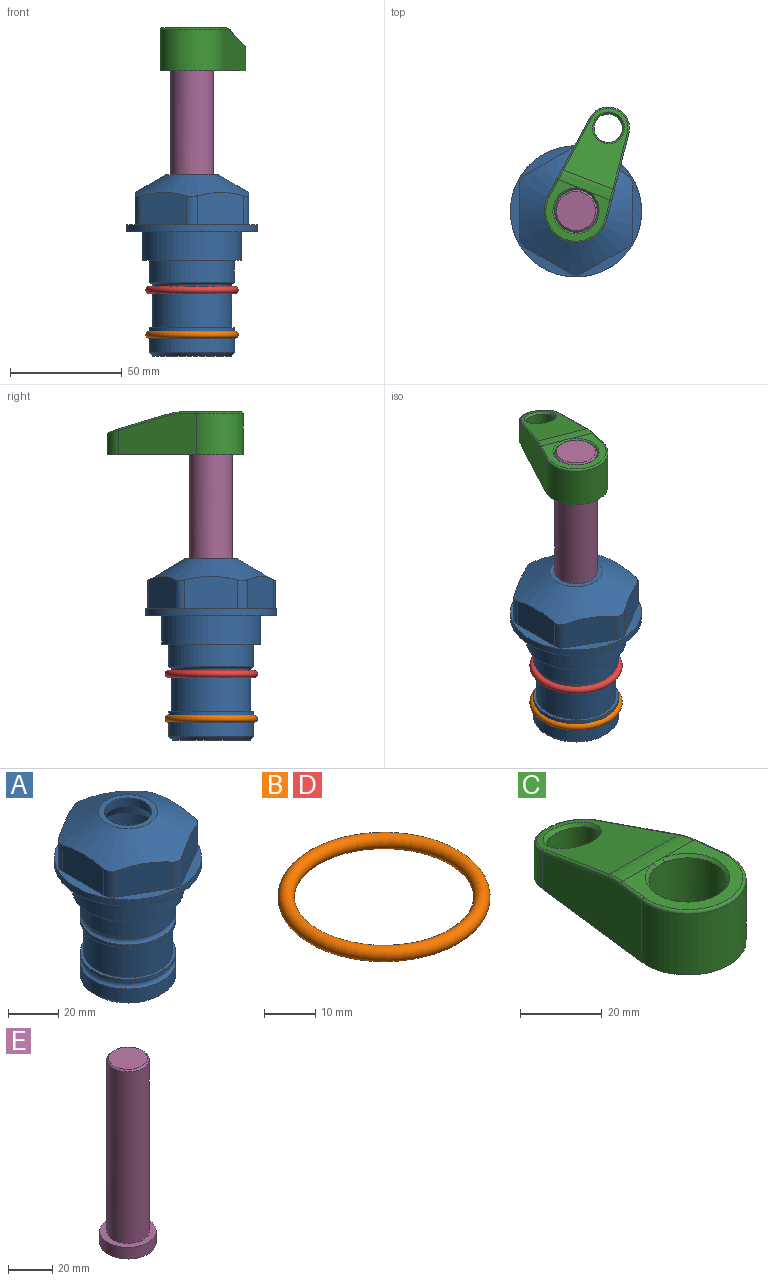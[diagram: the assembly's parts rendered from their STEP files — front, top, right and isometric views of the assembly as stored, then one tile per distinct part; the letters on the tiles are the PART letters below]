
ASSEMBLY  parts=5 mates=4
PART A: 36 faces, bbox 58.7x58.7x81 mm
  f0: cylinder r=17.78mm len=35.56mm, axis (0,0,1), area 1670.8mm2, adj f23,f24,f31
  f1: cylinder r=19.05mm len=38.1mm, axis (0,0,1), area 1191.9mm2, adj f26,f27,f30
  f2: plane 58.66x58.66mm, normal (0,0,-1), area 1150.6mm2, adj f3,f28
  f3: cylinder r=29.33mm len=58.66mm, axis (0,0,-1), area 585.1mm2, adj f2,f4
  f4: plane 58.66x58.66mm, normal (0,0,1), area 475.9mm2, adj f3,f5,f6,f7,f8,f9,f10,f11
  f5: plane 20.32x14.34mm, normal (-0.5,0.87,0), area 324.4mm2, adj f4,f15,f16,f17
  f6: plane 20.32x14.34mm, normal (0.5,0.87,0), area 324.4mm2, adj f4,f14,f15,f17
  f7: plane 23.48x14.34mm, normal (1,0,0), area 324.4mm2, adj f4,f13,f14,f17
  f8: plane 20.32x14.34mm, normal (0.5,-0.87,0), area 324.4mm2, adj f4,f12,f13,f17
  f9: plane 20.32x14.34mm, normal (-0.5,-0.87,0), area 324.4mm2, adj f4,f11,f12,f17
  f10: plane 23.48x14.34mm, normal (-1,0,0), area 324.4mm2, adj f4,f11,f16,f17
  f11: cylinder r=5.08mm len=12.85mm, axis (0,0,-1), area 67.2mm2, adj f4,f9,f10,f17
  f12: cylinder r=5.08mm len=12.85mm, axis (0,0,-1), area 67.2mm2, adj f4,f8,f9,f17
  f13: cylinder r=5.08mm len=12.85mm, axis (0,0,-1), area 67.2mm2, adj f4,f7,f8,f17
  f14: cylinder r=5.08mm len=12.85mm, axis (0,0,-1), area 67.2mm2, adj f4,f6,f7,f17
  f15: cylinder r=5.08mm len=12.85mm, axis (0,0,-1), area 67.2mm2, adj f4,f5,f6,f17
  f16: cylinder r=5.08mm len=12.85mm, axis (0,0,-1), area 67.2mm2, adj f4,f5,f10,f17
  f17: cone r=11.73mm half-angle=60deg, axis (0,0,-1), area 2071.8mm2, adj f5,f6,f7,f8,f9,f10,f11,f12
  f18: plane 23.46x23.46mm, normal (0,0,1), area 147.4mm2, adj f17,f35
  f19: plane 34.93x34.93mm, normal (0,0,-1), area 958mm2, adj f29
  f20: cylinder r=19.05mm len=38.1mm, axis (0,0,1), area 760.1mm2, adj f21,f29
  f21: torus R=19.05mm, axis (0,0,1), area 565.3mm2, adj f20,f22
  f22: cylinder r=19.05mm len=38.1mm, axis (0,0,1), area 190mm2, adj f21,f23
  f23: plane 38.1x38.1mm, normal (0,0,1), area 146.9mm2, adj f0,f22
  f24: plane 38.1x38.1mm, normal (0,0,-1), area 146.9mm2, adj f0,f25
  f25: cylinder r=19.05mm len=38.1mm, axis (0,0,1), area 190mm2, adj f24,f26
  f26: torus R=19.05mm, axis (0,0,1), area 565.3mm2, adj f1,f25
  f27: plane 44.45x44.45mm, normal (0,0,-1), area 411.7mm2, adj f1,f28
  f28: cylinder r=22.23mm len=44.45mm, axis (0,0,1), area 1773.5mm2, adj f2,f27
  f29: cone r=19.05mm half-angle=45deg, axis (0,0,1), area 257.5mm2, adj f19,f20
  f30: cylinder r=3.17mm len=6.75mm, axis (-1,0,0), area 128mm2, adj f1,f33
  f31: cylinder r=3.17mm len=6.35mm, axis (-1,0,0), area 102.5mm2, adj f0,f33
  f32: plane 25.4x25.4mm, normal (0,0,1), area 506.7mm2, adj f33
  f33: cylinder r=12.7mm len=66.42mm, axis (0,0,-1), area 5236.2mm2, adj f30,f31,f32,f34
  f34: cone r=9.53mm half-angle=30deg, axis (0,0,-1), area 443.4mm2, adj f33,f35
  f35: cylinder r=9.53mm len=19.05mm, axis (0,0,-1), area 240.9mm2, adj f18,f34
PART B: 1 faces, bbox 44.7x44.7x3.2 mm
  f0: torus R=19.05mm, axis (0,0,1), area 1193.9mm2
PART C: 31 faces, bbox 31.7x65.5x19.8 mm
  f0: plane 39.12x18.26mm, normal (0.99,0.12,0), area 612.2mm2, adj f1,f4,f7,f11,f13,f15
  f1: cylinder r=9.53mm len=18.91mm, axis (0,0,-1), area 296.1mm2, adj f0,f2,f7,f17
  f2: plane 39.12x18.26mm, normal (-0.99,0.12,0), area 612.2mm2, adj f1,f4,f7,f12,f14,f16
  f3: cylinder r=6.35mm len=12.7mm, axis (0,0,-1), area 362.4mm2, adj f7,f18
  f4: cylinder r=14.29mm len=28.58mm, axis (0,0,-1), area 882.2mm2, adj f0,f2,f7,f10
  f5: cylinder r=9.53mm len=19.05mm, axis (0,0,-1), area 1092.6mm2, adj f7,f19,f20
  f6: plane 26.99x23.69mm, normal (0,0,1), area 216.2mm2, adj f9,f10,f11,f12,f19
  f7: plane 63.5x28.58mm, normal (0,0,-1), area 661.8mm2, adj f0,f1,f2,f3,f4,f5,f22,f23
  f8: plane 33.52x23.6mm, normal (0,0.26,0.97), area 486mm2, adj f9,f15,f16,f17,f18
  f9: cylinder r=19.05mm len=24.72mm, axis (1,0,0), area 120.4mm2, adj f6,f8,f13,f14,f20
  f10: torus R=13.49mm, axis (0,0,1), area 59mm2, adj f4,f6,f11,f12
  f11: cylinder r=0.79mm len=8.67mm, axis (0.12,-0.99,0), area 10.8mm2, adj f0,f6,f10,f13
  f12: cylinder r=0.79mm len=8.67mm, axis (0.12,0.99,0), area 10.8mm2, adj f2,f6,f10,f14
  f13: bspline ~4.95x1.42mm, area 6.1mm2, adj f0,f9,f11,f15
  f14: bspline ~4.95x1.42mm, area 6.1mm2, adj f2,f9,f12,f16
  f15: cylinder r=0.79mm len=25.95mm, axis (0.12,-0.96,0.26), area 32.9mm2, adj f0,f8,f13,f17
  f16: cylinder r=0.79mm len=25.95mm, axis (0.12,0.96,-0.26), area 32.9mm2, adj f2,f8,f14,f17
  f17: bspline ~18.91x8.38mm, area 30mm2, adj f1,f8,f15,f16
  f18: bspline ~14.29x14.29mm, area 48.3mm2, adj f3,f8
  f19: cone r=9.53mm half-angle=45deg, axis (0,0,1), area 66.5mm2, adj f5,f6,f20
  f20: bspline ~3.22x0.96mm, area 3.5mm2, adj f5,f9,f19
  f21: plane 2.75x2.72mm, normal (0,0,-1), area 2.9mm2, adj f23,f25,f28
  f22: plane 23.05x15.88mm, normal (-0.99,-0.12,0), area 323.6mm2, adj f7,f25,f26,f27,f28,f29
  f23: plane 23.05x15.88mm, normal (0.99,-0.12,0), area 323.6mm2, adj f7,f21,f25,f27,f28,f30
  f24: cylinder r=9.53mm len=10.69mm, axis (0,0,-1), area 114.7mm2, adj f7,f27,f29,f30
  f25: cylinder r=12.7mm len=20.59mm, axis (0,0,-1), area 381.1mm2, adj f7,f21,f22,f23,f26,f28
  f26: plane 2.75x2.72mm, normal (0,0,-1), area 2.9mm2, adj f22,f25,f28
  f27: plane 19.72x18.37mm, normal (0,-0.26,-0.97), area 291.8mm2, adj f22,f23,f24,f28,f29,f30
  f28: cylinder r=15.88mm len=19.92mm, axis (1,0,0), area 54.8mm2, adj f21,f22,f23,f25,f26,f27
  f29: cylinder r=1.59mm len=11mm, axis (0,0,-1), area 34.7mm2, adj f7,f22,f24,f27
  f30: cylinder r=1.59mm len=11mm, axis (0,0,-1), area 34.7mm2, adj f7,f23,f24,f27
PART D: same geometry as B
PART E: 6 faces, bbox 25.4x25.4x101.6 mm
  f0: plane 17.46x17.46mm, normal (0,0,1), area 239.5mm2, adj f5
  f1: plane 25.4x25.4mm, normal (0,0,-1), area 506.7mm2, adj f2
  f2: cylinder r=12.7mm len=25.4mm, axis (0,0,1), area 506.7mm2, adj f1,f3
  f3: plane 25.4x25.4mm, normal (0,0,1), area 221.7mm2, adj f2,f4
  f4: cylinder r=9.53mm len=94.46mm, axis (0,0,1), area 5653mm2, adj f3,f5
  f5: cone r=8.73mm half-angle=45deg, axis (0,0,-1), area 64.4mm2, adj f0,f4
PLACE A at identity fixed
PLACE B t=(0,0,-21.59)mm
PLACE C rot(axis=(0,0,-1),21.3deg) t=(0,0,27.55)mm
PLACE D t=(0,0,-1.59)mm
PLACE E rot(axis=(0,0,-1),21.3deg) t=(0,0,27.55)mm
MATE fastened D.f0 <-> A.f0  axis (0,0,1) through (0,0,-26.1)mm
MATE fastened B.f0 <-> A.f0  axis (0,0,1) through (0,0,-46.1)mm
MATE fastened E.f2 <-> C.f4  axis (0,0,1) through (0,0,91.05)mm
MATE cylindrical E.f2 <-> A.f0  axis (0,0,-1) through (0,0,-10.55)mm
